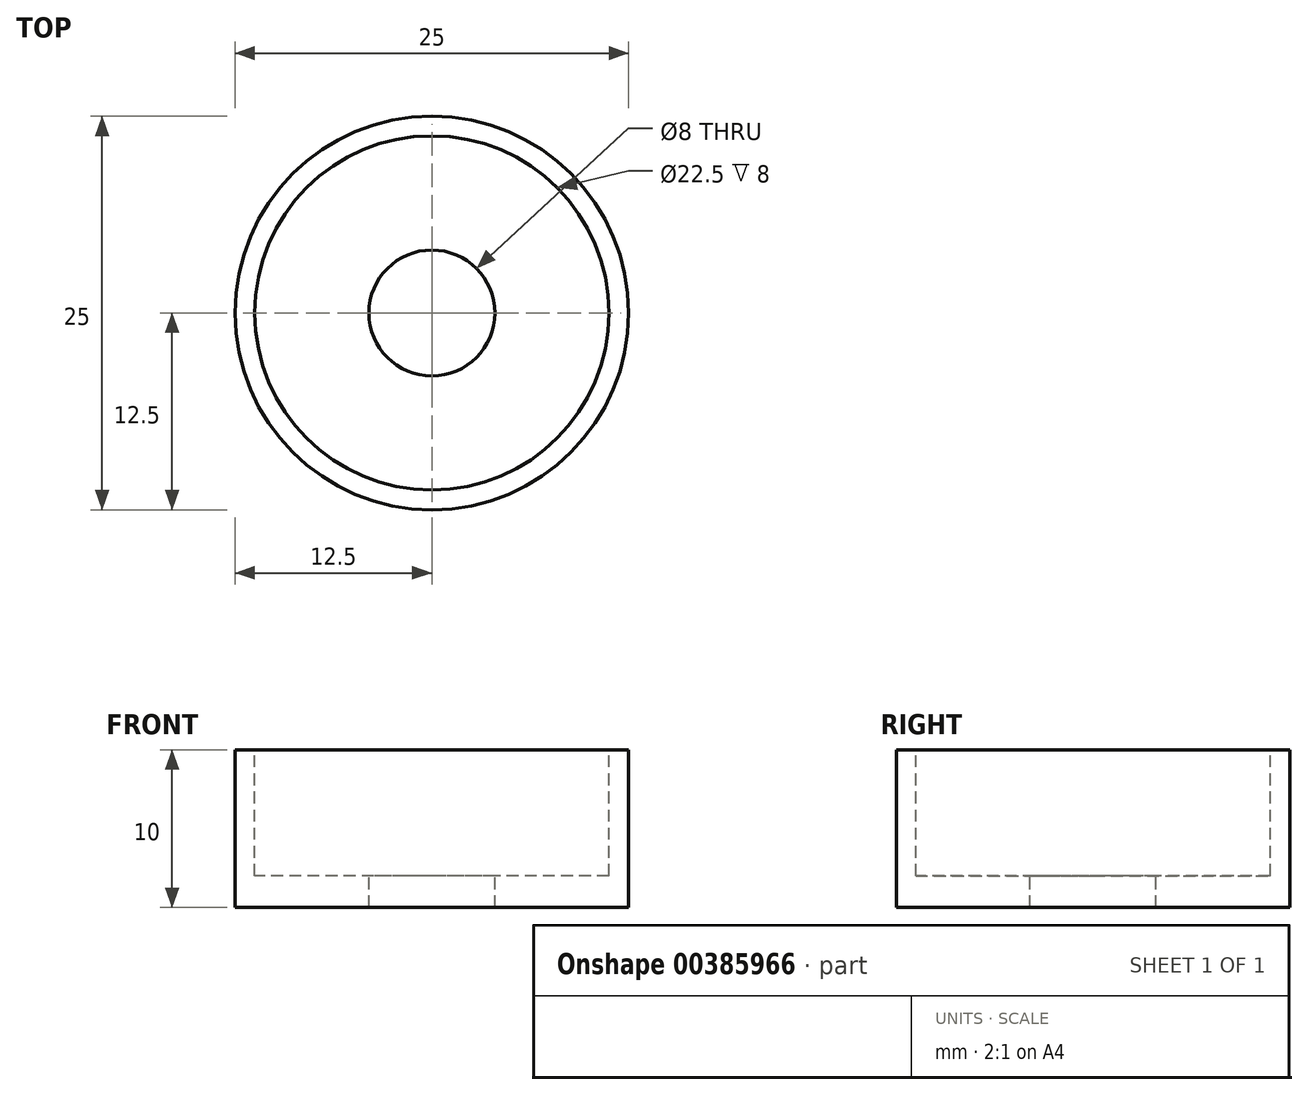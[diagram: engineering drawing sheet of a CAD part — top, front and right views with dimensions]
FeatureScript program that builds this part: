
annotation { "Feature Type Name" : "Feature", "Feature Type Description" : "" }
export const myFeature = defineFeature(function(context is Context, id is Id, definition is map)
    precondition{}
    {
        {
            var Q0;
            Q0=qCreatedBy(makeId("Top.planeOp"),FACE);
            var sketch = newSketch(context, id + "F0", { "sketchPlane" : qUnion([Q0])});
            skCircle(sketch, "E0", {"center": v(0, 0) * mm, "radius": 12.5 * mm});
            skSolve(sketch);
        }
        {
            var Q0;
            Q0=qSketchRegion(id+"F0",true);
            extrude(context, id + "F1", {"entities" : qUnion([Q0]), "depth" : 10 * mm, "offsetDistance" : 25 * mm});
        }
        {
            var Q0;
            Q0=makeQuery(id+"F1.opExtrude","CAP_FACE",FACE,{"disambiguationData":[OSD([sQuery(id+"F0.wireOp",EDGE,"E0")])],"isStart":false});
            var sketch = newSketch(context, id + "F2", { "sketchPlane" : qUnion([Q0])});
            skCircle(sketch, "E1", {"center": v(0, 0) * mm, "radius": 11.25 * mm});
            skCircle(sketch, "E2", {"center": v(0, 0) * mm, "radius": 4 * mm});
            skSolve(sketch);
        }
        {
            var Q0;
            Q0=makeQuery(id+"F2.imprint","IMPRINT",FACE,{"disambiguationData":[TD([[makeQuery(id+"F2.imprint","IMPRINT",EDGE,{"derivedFrom":sQuery(id+"F2.wireOp",EDGE,"E2")}),1.0]])]});
            extrude(context, id + "F3", {"entities" : qUnion([Q0]), "operationType" : NewBodyOperationType.REMOVE, "oppositeDirection" : true, "depth" : 25 * mm, "offsetDistance" : 25 * mm});
        }
        {
            var Q0;
            Q0=makeQuery(id+"F2.imprint","IMPRINT",FACE,{"disambiguationData":[TD([[makeQuery(id+"F2.imprint","IMPRINT",EDGE,{"derivedFrom":sQuery(id+"F2.wireOp",EDGE,"E1")}),1.0]])]});
            extrude(context, id + "F4", {"entities" : qUnion([Q0]), "operationType" : NewBodyOperationType.REMOVE, "oppositeDirection" : true, "depth" : 8 * mm, "offsetDistance" : 25 * mm});
        }
    });
